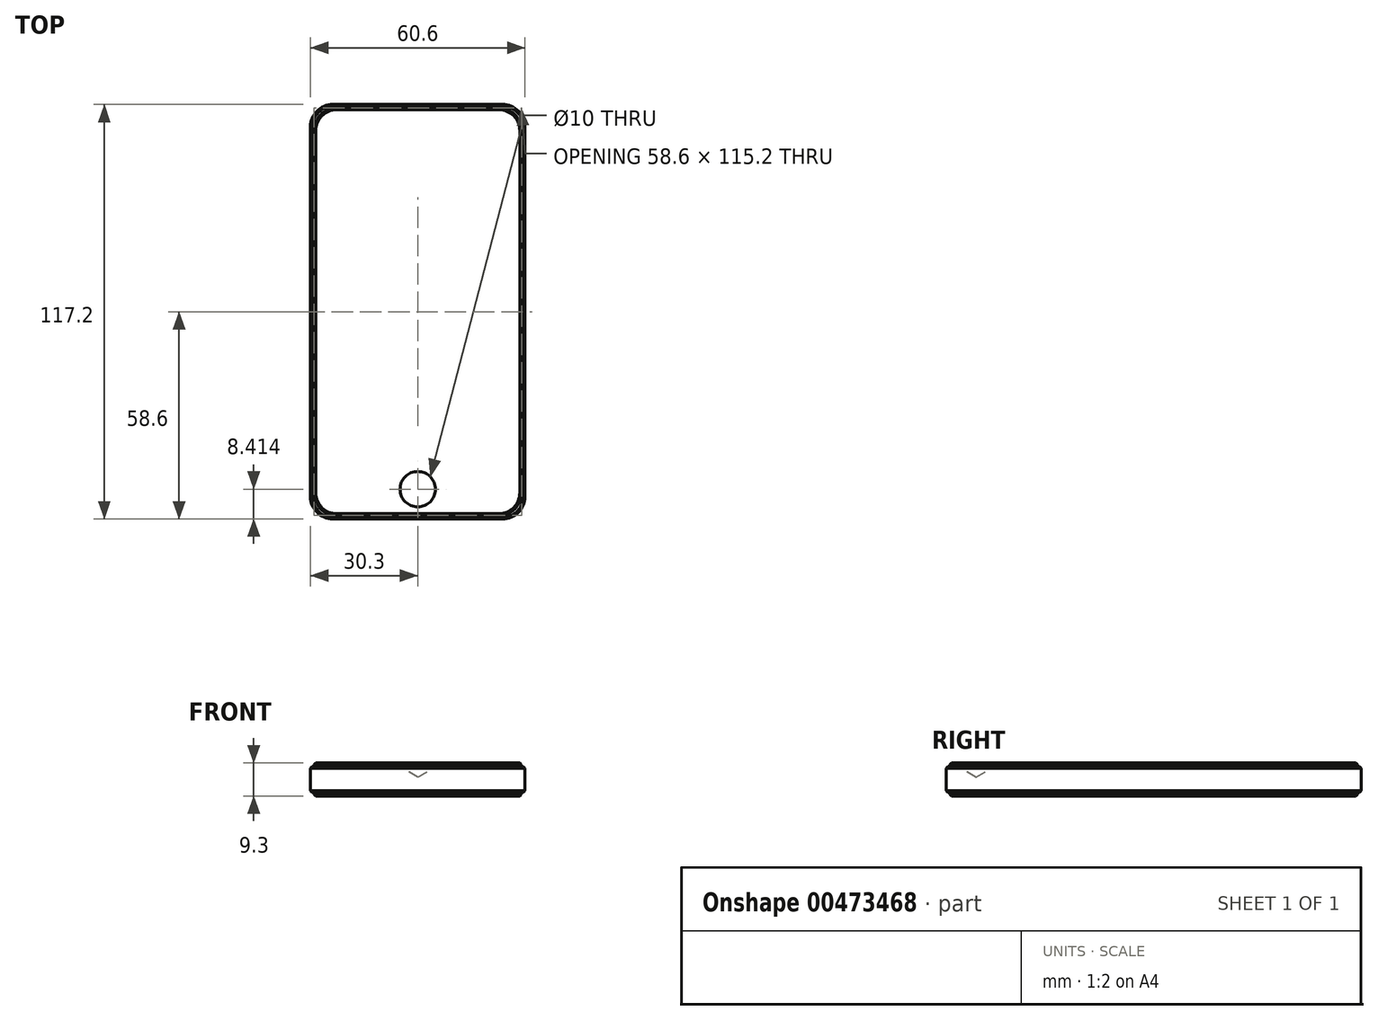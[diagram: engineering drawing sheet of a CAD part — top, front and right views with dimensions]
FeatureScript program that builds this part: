
annotation { "Feature Type Name" : "Feature", "Feature Type Description" : "" }
export const myFeature = defineFeature(function(context is Context, id is Id, definition is map)
    precondition{}
    {
        {
            var Q0;
            Q0=qCreatedBy(makeId("Top.planeOp"),FACE);
            var sketch = newSketch(context, id + "F0", { "sketchPlane" : qUnion([Q0])});
            skLineSegment(sketch, "E0.bottom", {"start": v(22.95, -57.6) * mm, "end": v(-22.95, -57.6) * mm});
            skLineSegment(sketch, "E0.top", {"start": v(22.95, 57.6) * mm, "end": v(-22.95, 57.6) * mm});
            skLineSegment(sketch, "E0.left", {"start": v(29.3, -51.25) * mm, "end": v(29.3, 51.25) * mm});
            skLineSegment(sketch, "E0.right", {"start": v(-29.3, -51.25) * mm, "end": v(-29.3, 51.25) * mm});
            skPoint(sketch, "E0.middle", {"position": v(0, 0) * mm});
            skPoint(sketch, "E1.visualSharp", {"position": v(-29.3, -57.6) * mm});
            skArc(sketch, "E1.filletArc", {"start": v(-29.3, -51.25) * mm, "mid": v(-27.44, -55.74) * mm, "end": v(-22.95, -57.6) * mm});
            skPoint(sketch, "E2.visualSharp", {"position": v(-29.3, 57.6) * mm});
            skArc(sketch, "E2.filletArc", {"start": v(-22.95, 57.6) * mm, "mid": v(-27.44, 55.74) * mm, "end": v(-29.3, 51.25) * mm});
            skPoint(sketch, "E3.visualSharp", {"position": v(29.3, 57.6) * mm});
            skArc(sketch, "E3.filletArc", {"start": v(29.3, 51.25) * mm, "mid": v(27.44, 55.74) * mm, "end": v(22.95, 57.6) * mm});
            skPoint(sketch, "E4.visualSharp", {"position": v(29.3, -57.6) * mm});
            skArc(sketch, "E4.filletArc", {"start": v(22.95, -57.6) * mm, "mid": v(27.44, -55.74) * mm, "end": v(29.3, -51.25) * mm});
            skSolve(sketch);
        }
        {
            var Q0;
            Q0=makeQuery(id+"F0.imprint","IMPRINT",FACE,{"disambiguationData":[TD([[makeQuery(id+"F0.imprint","IMPRINT",EDGE,{"derivedFrom":sQuery(id+"F0.wireOp",EDGE,"E0.bottom")}),-1.0]])]});
            extrude(context, id + "F1", {"entities" : qUnion([Q0]), "endBound" : BoundingType.SYMMETRIC, "depth" : 9.3 * mm});
        }
        {
            var Q0;
            Q0=qCreatedBy(makeId("Top.planeOp"),FACE);
            var sketch = newSketch(context, id + "F2", { "sketchPlane" : qUnion([Q0])});
            skLineSegment(sketch, "E5.bottom", {"start": v(23.95, -58.6) * mm, "end": v(-23.95, -58.6) * mm});
            skLineSegment(sketch, "E5.top", {"start": v(23.95, 58.6) * mm, "end": v(-23.95, 58.6) * mm});
            skLineSegment(sketch, "E5.left", {"start": v(30.3, -52.25) * mm, "end": v(30.3, 52.25) * mm});
            skLineSegment(sketch, "E5.right", {"start": v(-30.3, -52.25) * mm, "end": v(-30.3, 52.25) * mm});
            skPoint(sketch, "E5.middle", {"position": v(0, 0) * mm});
            skPoint(sketch, "E6.visualSharp", {"position": v(-30.3, 58.6) * mm});
            skArc(sketch, "E6.filletArc", {"start": v(-23.95, 58.6) * mm, "mid": v(-28.44, 56.74) * mm, "end": v(-30.3, 52.25) * mm});
            skPoint(sketch, "E7.visualSharp", {"position": v(30.3, 58.6) * mm});
            skArc(sketch, "E7.filletArc", {"start": v(30.3, 52.25) * mm, "mid": v(28.44, 56.74) * mm, "end": v(23.95, 58.6) * mm});
            skPoint(sketch, "E8.visualSharp", {"position": v(30.3, -58.6) * mm});
            skArc(sketch, "E8.filletArc", {"start": v(23.95, -58.6) * mm, "mid": v(28.44, -56.74) * mm, "end": v(30.3, -52.25) * mm});
            skPoint(sketch, "E9.visualSharp", {"position": v(-30.3, -58.6) * mm});
            skArc(sketch, "E9.filletArc", {"start": v(-30.3, -52.25) * mm, "mid": v(-28.44, -56.74) * mm, "end": v(-23.95, -58.6) * mm});
            skSolve(sketch);
        }
        {
            var Q0;
            Q0=makeQuery(id+"F2.imprint","IMPRINT",FACE,{"disambiguationData":[TD([[makeQuery(id+"F2.imprint","IMPRINT",EDGE,{"derivedFrom":sQuery(id+"F2.wireOp",EDGE,"E5.bottom")}),-1.0]])]});
            extrude(context, id + "F3", {"entities" : qUnion([Q0]), "operationType" : NewBodyOperationType.ADD, "endBound" : BoundingType.SYMMETRIC, "depth" : 7.3 * mm});
        }
        {
            var Q0;
            Q0=makeQuery(id+"F3.opExtrude","CAP_EDGE",EDGE,{"disambiguationData":[OSD([sQuery(id+"F2.wireOp",EDGE,"E5.right")])],"isStart":false});
            chamfer(context, id + "F4", {"entities" : qUnion([Q0]), "width" : 0.5 * mm, "tangentPropagation" : true});
        }
        {
            var Q0;
            Q0=makeQuery(id+"F3.opExtrude","CAP_EDGE",EDGE,{"disambiguationData":[OSD([sQuery(id+"F2.wireOp",EDGE,"E5.right")])],"isStart":true});
            chamfer(context, id + "F5", {"entities" : qUnion([Q0]), "width" : 0.5 * mm, "tangentPropagation" : true});
        }
        {
            var Q0;
            Q0=makeQuery(id+"F1.opExtrude","CAP_EDGE",EDGE,{"disambiguationData":[OSD([sQuery(id+"F0.wireOp",EDGE,"E0.right")])],"isStart":false});
            chamfer(context, id + "F6", {"entities" : qUnion([Q0]), "width" : 0.5 * mm, "tangentPropagation" : true});
        }
        {
            var Q0;
            Q0=makeQuery(id+"F1.opExtrude","CAP_EDGE",EDGE,{"disambiguationData":[OSD([sQuery(id+"F0.wireOp",EDGE,"E0.left")])],"isStart":true});
            chamfer(context, id + "F7", {"entities" : qUnion([Q0]), "width" : 0.5 * mm, "tangentPropagation" : true});
        }
        {
            var Q0;
            Q0=makeQuery(id+"F1.opExtrude","CAP_FACE",FACE,{"disambiguationData":[OSD([sQuery(id+"F0.wireOp",EDGE,"E0.bottom"),sQuery(id+"F0.wireOp",EDGE,"E0.top"),sQuery(id+"F0.wireOp",EDGE,"E0.left"),sQuery(id+"F0.wireOp",EDGE,"E0.right"),sQuery(id+"F0.wireOp",EDGE,"E1.filletArc"),sQuery(id+"F0.wireOp",EDGE,"E2.filletArc"),sQuery(id+"F0.wireOp",EDGE,"E3.filletArc"),sQuery(id+"F0.wireOp",EDGE,"E4.filletArc")])],"isStart":false});
            var sketch = newSketch(context, id + "F8", { "sketchPlane" : qUnion([Q0])});
            skPoint(sketch, "E10", {"position": v(0, -50.19) * mm});
            skSolve(sketch);
        }
        {
            var Q0;
            Q0=sQuery(id+"F8.wireOp",VERTEX,"E10");
            var Q1;
            Q1=makeQuery(id+"F1.opExtrude","SWEPT_BODY",BODY,{"disambiguationData":[OSD([sQuery(id+"F0.wireOp",EDGE,"E0.bottom"),sQuery(id+"F0.wireOp",EDGE,"E0.top"),sQuery(id+"F0.wireOp",EDGE,"E0.left"),sQuery(id+"F0.wireOp",EDGE,"E0.right"),sQuery(id+"F0.wireOp",EDGE,"E1.filletArc"),sQuery(id+"F0.wireOp",EDGE,"E2.filletArc"),sQuery(id+"F0.wireOp",EDGE,"E3.filletArc"),sQuery(id+"F0.wireOp",EDGE,"E4.filletArc")])]});
            hole(context, id + "F9", {"style" : HoleStyle.SIMPLE, "endStyle" : HoleEndStyle.BLIND, "holeDiameter" : 10 * mm, "holeDepth" : 1 * mm, "isTappedThrough" : true, "tappedDepth" : 12.7 * mm, "tapClearance" : 3, "locations" : qUnion([Q0]), "scope" : qUnion([Q1])});
        }
    });
